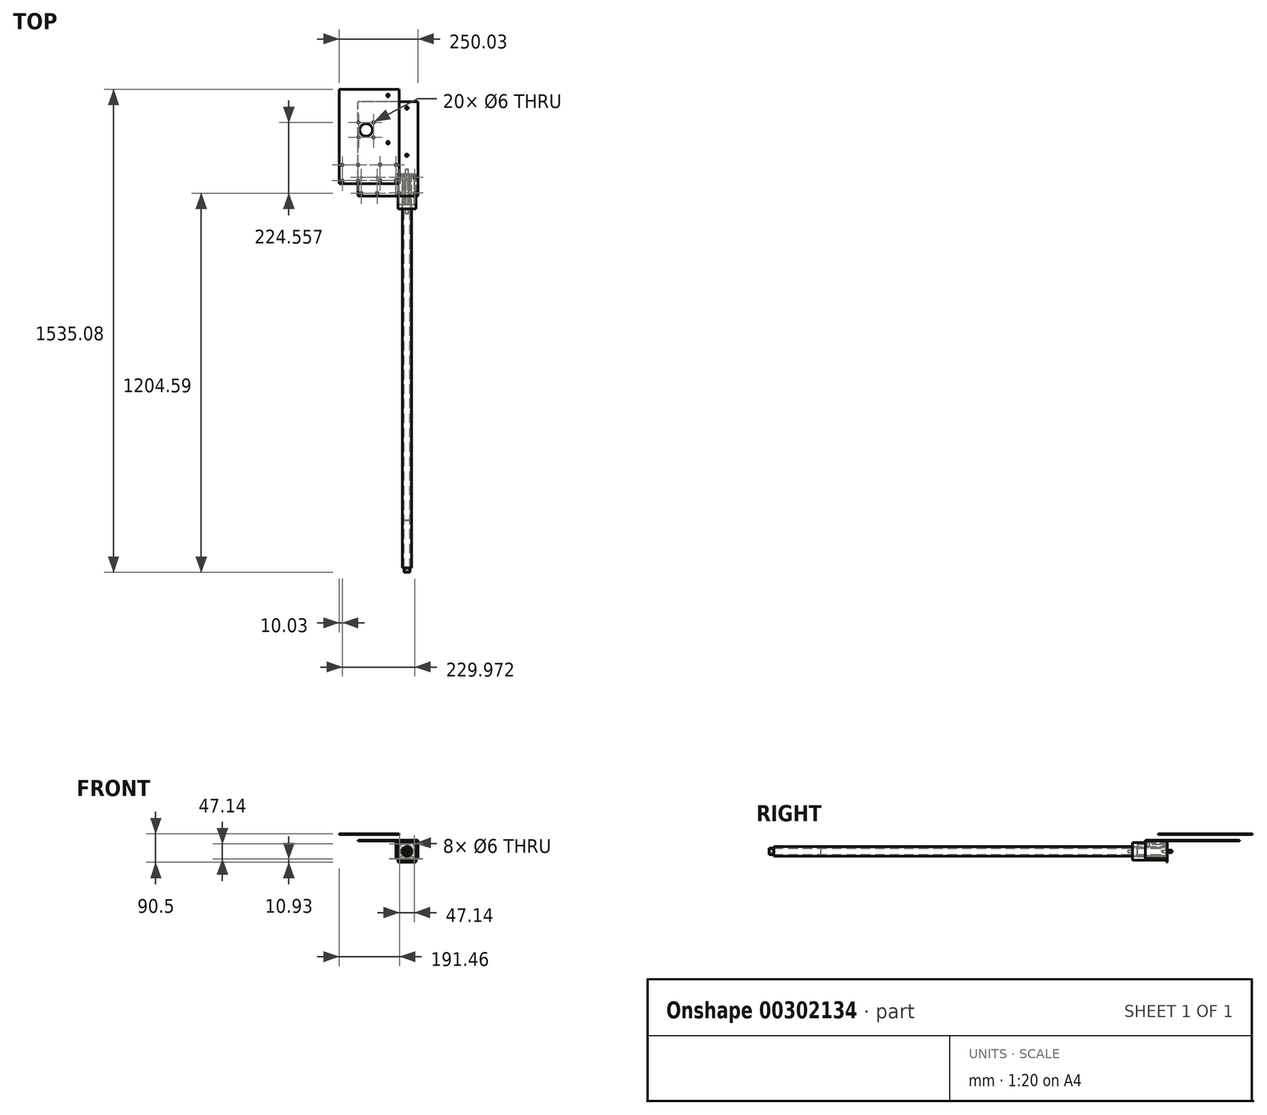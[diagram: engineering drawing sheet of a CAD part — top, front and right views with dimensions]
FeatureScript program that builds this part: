
annotation { "Feature Type Name" : "Feature", "Feature Type Description" : "" }
export const myFeature = defineFeature(function(context is Context, id is Id, definition is map)
    precondition{}
    {
        {
            var Q0;
            Q0=qCreatedBy(makeId("Front.planeOp"),FACE);
            var sketch = newSketch(context, id + "F0", { "sketchPlane" : qUnion([Q0])});
            skPoint(sketch, "E0.middle", {"position": v(0, 0) * mm});
            skLineSegment(sketch, "E1.bottom", {"start": v(28.5, 28.5) * mm, "end": v(-28.5, 28.5) * mm});
            skLineSegment(sketch, "E1.top", {"start": v(28.5, -28.5) * mm, "end": v(-28.5, -28.5) * mm});
            skLineSegment(sketch, "E1.left", {"start": v(28.5, 28.5) * mm, "end": v(28.5, -28.5) * mm});
            skLineSegment(sketch, "E1.right", {"start": v(-28.5, 28.5) * mm, "end": v(-28.5, -28.5) * mm});
            skCircle(sketch, "E2", {"center": v(0, 0) * mm, "radius": 4 * mm});
            skLineSegment(sketch, "E3.bottom", {"start": v(23.5, 23.5) * mm, "end": v(-23.5, 23.5) * mm, "construction": true});
            skLineSegment(sketch, "E3.top", {"start": v(23.5, -23.5) * mm, "end": v(-23.5, -23.5) * mm, "construction": true});
            skLineSegment(sketch, "E3.left", {"start": v(23.5, 23.5) * mm, "end": v(23.5, -23.5) * mm, "construction": true});
            skLineSegment(sketch, "E3.right", {"start": v(-23.5, 23.5) * mm, "end": v(-23.5, -23.5) * mm, "construction": true});
            skSolve(sketch);
        }
        {
            var Q0;
            Q0=makeQuery(id+"F0.imprint","IMPRINT",FACE,{"disambiguationData":[TD([[makeQuery(id+"F0.imprint","IMPRINT",EDGE,{"derivedFrom":sQuery(id+"F0.wireOp",EDGE,"E2")}),1.0]])]});
            var Q1;
            Q1=sQuery(id+"F0.wireOp",EDGE,"E2");
            extrude(context, id + "F1", {"entities" : qUnion([Q0]), "surfaceEntities" : qUnion([Q1]), "depth" : 125 * mm, "hasSecondDirection" : true, "secondDirectionOppositeDirection" : true, "secondDirectionDepth" : 15 * mm});
        }
        {
            var Q0;
            Q0=makeQuery(id+"F0.imprint","IMPRINT",FACE,{"disambiguationData":[TD([[makeQuery(id+"F0.imprint","IMPRINT",EDGE,{"derivedFrom":sQuery(id+"F0.wireOp",EDGE,"E1.bottom")}),1.0]])]});
            extrude(context, id + "F2", {"entities" : qUnion([Q0]), "operationType" : NewBodyOperationType.ADD, "depth" : 110 * mm});
        }
        {
            var Q0;
            Q0=sQuery(id+"F0.wireOp",VERTEX,"E3.left.end");
            var Q1;
            Q1=sQuery(id+"F0.wireOp",VERTEX,"E3.left.start");
            var Q2;
            Q2=sQuery(id+"F0.wireOp",VERTEX,"E3.right.start");
            var Q3;
            Q3=sQuery(id+"F0.wireOp",VERTEX,"E3.right.end");
            var Q4;
            Q4=makeQuery(id+"F1.opExtrude","SWEPT_BODY",BODY,{"disambiguationData":[OSD([sQuery(id+"F0.wireOp",EDGE,"E2")])]});
            hole(context, id + "F3", {"style" : HoleStyle.SIMPLE, "endStyle" : HoleEndStyle.BLIND, "oppositeDirection" : true, "standardTappedOrClearance" : lookupTablePath({ "standard" : "ISO", "size" : "6", "type" : "Drilled" }), "standardBlindInLast" : lookupTablePath({ "standard" : "ISO", "size" : "6", "type" : "Drilled" }), "holeDiameter" : 6 * mm, "holeDepth" : 16 * mm, "tappedDepth" : 12 * mm, "tapClearance" : 3, "locations" : qUnion([Q0, Q1, Q2, Q3]), "scope" : qUnion([Q4])});
        }
        {
            var Q0;
            Q0=qCreatedBy(makeId("Front.planeOp"),FACE);
            var sketch = newSketch(context, id + "F4", { "sketchPlane" : qUnion([Q0])});
            skCircle(sketch, "E4", {"center": v(0, 0) * mm, "radius": 12.5 * mm});
            skSolve(sketch);
        }
        {
            var Q0;
            Q0 = qSketchRegion(id + "F4", true);
            extrude(context, id + "F5", {"entities" : qUnion([Q0]), "depth" : (1100) * mm});
        }
        {
            var Q0;
            Q0=qCreatedBy(makeId("Front.planeOp"),FACE);
            var sketch = newSketch(context, id + "F6", { "sketchPlane" : qUnion([Q0])});
            skLineSegment(sketch, "E5.top", {"start": v(0, 33) * mm, "end": v(35, 33) * mm});
            skLineSegment(sketch, "E5.left", {"start": v(0, 15) * mm, "end": v(0, 33) * mm});
            skLineSegment(sketch, "E5.right", {"start": v(35, 0) * mm, "end": v(35, 33) * mm});
            skLineSegment(sketch, "E6.top", {"start": v(7, -23) * mm, "end": v(35, -23) * mm});
            skLineSegment(sketch, "E6.right", {"start": v(35, 0) * mm, "end": v(35, -23) * mm});
            skLineSegment(sketch, "E7.MirrorCS", {"start": v(0, 33) * mm, "end": v(-35, 33) * mm});
            skLineSegment(sketch, "E8.MirrorCS", {"start": v(-35, 0) * mm, "end": v(-35, 33) * mm});
            skLineSegment(sketch, "E9.MirrorCS", {"start": v(-35, 0) * mm, "end": v(-35, -23) * mm});
            skLineSegment(sketch, "E10.MirrorCS", {"start": v(-7, -23) * mm, "end": v(-35, -23) * mm});
            skCircle(sketch, "E11", {"center": v(0, 0) * mm, "radius": 15 * mm});
            skLineSegment(sketch, "E12", {"start": v(7, -23) * mm, "end": v(4.37, -14.35) * mm});
            skLineSegment(sketch, "E13", {"start": v(-4.37, -14.35) * mm, "end": v(-7, -23) * mm});
            skPoint(sketch, "E14.orphan", {"position": v(0, -23) * mm});
            skSolve(sketch);
        }
        {
            var Q0;
            Q0=makeQuery(id+"F6.imprint","IMPRINT",FACE,{"disambiguationData":[TD([[makeQuery(id+"F6.imprint","IMPRINT",EDGE,{"derivedFrom":sQuery(id+"F6.wireOp",EDGE,"E5.top")}),-1.0]])]});
            var Q1;
            {var subQ0=sQuery(id+"F6.wireOp",EDGE,"E5.left");Q1=makeQuery(id+"F6.imprint","IMPRINT",FACE,{"disambiguationData":[TD([[makeQuery(id+"F6.imprint","IMPRINT",EDGE,{"derivedFrom":subQ0}),1.0]])]});}
            extrude(context, id + "F7", {"entities" : qUnion([Q0, Q1]), "depth" : 70 * mm});
        }
        {
            var Q0;
            Q0=qCreatedBy(makeId("Front.planeOp"),FACE);
            var sketch = newSketch(context, id + "F8", { "sketchPlane" : qUnion([Q0])});
            skLineSegment(sketch, "E15.top", {"start": v(0, 23) * mm, "end": v(24, 23) * mm});
            skLineSegment(sketch, "E15.right", {"start": v(24, 0) * mm, "end": v(24, 23) * mm});
            skLineSegment(sketch, "E16.top", {"start": v(5, -16) * mm, "end": v(24, -16) * mm});
            skLineSegment(sketch, "E16.right", {"start": v(24, 0) * mm, "end": v(24, -16) * mm});
            skLineSegment(sketch, "E17.MirrorCS", {"start": v(0, 23) * mm, "end": v(-24, 23) * mm});
            skLineSegment(sketch, "E18.MirrorCS", {"start": v(-24, 0) * mm, "end": v(-24, 23) * mm});
            skLineSegment(sketch, "E19.MirrorCS", {"start": v(-24, 0) * mm, "end": v(-24, -16) * mm});
            skLineSegment(sketch, "E20.MirrorCS", {"start": v(-5, -16) * mm, "end": v(-24, -16) * mm});
            skArc(sketch, "E21", {"start": v(2.98, -9.54) * mm, "mid": v(0, 10) * mm, "end": v(-2.98, -9.54) * mm});
            skLineSegment(sketch, "E22", {"start": v(2.98, -9.54) * mm, "end": v(5, -16) * mm});
            skLineSegment(sketch, "E23", {"start": v(-5, -16) * mm, "end": v(-2.98, -9.54) * mm});
            skPoint(sketch, "E24.orphan", {"position": v(5, 0) * mm});
            skPoint(sketch, "E25.MirrorCS.start.orphan", {"position": v(-5, 0) * mm});
            skPoint(sketch, "E26.orphan", {"position": v(0, -16) * mm});
            skSolve(sketch);
        }
        {
            var Q0;
            Q0=makeQuery(id+"F8.imprint","IMPRINT",FACE,{"disambiguationData":[TD([[makeQuery(id+"F8.imprint","IMPRINT",EDGE,{"derivedFrom":sQuery(id+"F8.wireOp",EDGE,"E15.top")}),-1.0]])]});
            extrude(context, id + "F9", {"entities" : qUnion([Q0]), "depth" : 96 * mm});
        }
        {
            var Q0;
            Q0=makeQuery(id+"F7.opExtrude","SWEPT_FACE",FACE,{"disambiguationData":[OSD([sQuery(id+"F6.wireOp",EDGE,"E5.top"),sQuery(id+"F6.wireOp",EDGE,"E7.MirrorCS")])]});
            var sketch = newSketch(context, id + "F10", { "sketchPlane" : qUnion([Q0])});
            skLineSegment(sketch, "E27.bottom", {"start": v(-25, -10) * mm, "end": v(25, -10) * mm, "construction": true});
            skLineSegment(sketch, "E27.top", {"start": v(-25, -60) * mm, "end": v(25, -60) * mm, "construction": true});
            skLineSegment(sketch, "E27.left", {"start": v(-25, -10) * mm, "end": v(-25, -60) * mm, "construction": true});
            skLineSegment(sketch, "E27.right", {"start": v(25, -10) * mm, "end": v(25, -60) * mm, "construction": true});
            skSolve(sketch);
        }
        {
            var Q0;
            Q0=sQuery(id+"F10.wireOp",VERTEX,"E27.left.end");
            var Q1;
            Q1=sQuery(id+"F10.wireOp",VERTEX,"E27.bottom.start");
            var Q2;
            Q2=sQuery(id+"F10.wireOp",VERTEX,"E27.right.start");
            var Q3;
            Q3=sQuery(id+"F10.wireOp",VERTEX,"E27.right.end");
            var Q4;
            Q4=makeQuery(id+"F7.opExtrude","SWEPT_BODY",BODY,{"disambiguationData":[OSD([sQuery(id+"F6.wireOp",EDGE,"E5.top"),sQuery(id+"F6.wireOp",EDGE,"E5.right"),sQuery(id+"F6.wireOp",EDGE,"E6.top"),sQuery(id+"F6.wireOp",EDGE,"E6.right"),sQuery(id+"F6.wireOp",EDGE,"E7.MirrorCS"),sQuery(id+"F6.wireOp",EDGE,"E8.MirrorCS"),sQuery(id+"F6.wireOp",EDGE,"E9.MirrorCS"),sQuery(id+"F6.wireOp",EDGE,"E10.MirrorCS"),sQuery(id+"F6.wireOp",EDGE,"E11"),sQuery(id+"F6.wireOp",EDGE,"E12"),sQuery(id+"F6.wireOp",EDGE,"E13")])]});
            hole(context, id + "F11", {"style" : HoleStyle.SIMPLE, "endStyle" : HoleEndStyle.BLIND, "standardTappedOrClearance" : lookupTablePath({ "standard" : "ISO", "size" : "8", "type" : "Drilled" }), "standardBlindInLast" : lookupTablePath({ "standard" : "ISO", "size" : "8", "type" : "Drilled" }), "holeDiameter" : 8 * mm, "holeDepth" : 16 * mm, "tappedDepth" : 12 * mm, "tapClearance" : 3, "locations" : qUnion([Q0, Q1, Q2, Q3]), "scope" : qUnion([Q4])});
        }
        {
            var Q0;
            Q0=qCreatedBy(makeId("Front.planeOp"),FACE);
            var sketch = newSketch(context, id + "F12", { "sketchPlane" : qUnion([Q0])});
            skCircle(sketch, "E28", {"center": v(0, 0) * mm, "radius": 15 * mm});
            skSolve(sketch);
        }
        {
            var Q0;
            Q0=makeQuery(id+"F12.imprint","IMPRINT",FACE,{"disambiguationData":[TD([[makeQuery(id+"F12.imprint","IMPRINT",EDGE,{"derivedFrom":sQuery(id+"F12.wireOp",EDGE,"E28")}),1.0]])]});
            extrude(context, id + "F13", {"entities" : qUnion([Q0]), "depth" : 1250 * mm});
        }
        {
            var Q0;
            {var subQ0=sQuery(id+"F6.wireOp",EDGE,"E5.top");Q0=makeQuery(id+"F10.imprint","IMPRINT",FACE,{"disambiguationData":[TD([[makeQuery(id+"F10.imprint","IMPRINT",EDGE,{"derivedFrom":makeQuery(id+"F7.opExtrude","SWEPT_EDGE",EDGE,{"disambiguationData":[OSD([subQ0,sQuery(id+"F6.wireOp",EDGE,"E5.right")])]})}),1.0]])]});}
            var sketch = newSketch(context, id + "F14", { "sketchPlane" : qUnion([Q0])});
            skLineSegment(sketch, "E29.left", {"start": v(0, -59.92) * mm, "end": v(0, -9.92) * mm});
            skLineSegment(sketch, "E30.bottom", {"start": v(-145, -10.41) * mm, "end": v(-95, -10.41) * mm, "construction": true});
            skLineSegment(sketch, "E30.top", {"start": v(-145, -60.41) * mm, "end": v(-95, -60.41) * mm, "construction": true});
            skLineSegment(sketch, "E30.left", {"start": v(-145, -10.41) * mm, "end": v(-145, -60.41) * mm, "construction": true});
            skLineSegment(sketch, "E30.right", {"start": v(-95, -10.41) * mm, "end": v(-95, -60.41) * mm, "construction": true});
            skPoint(sketch, "E30.middle", {"position": v(-120, -35.41) * mm});
            skLineSegment(sketch, "E31.bottom", {"start": v(34.97, -69.92) * mm, "end": v(-155.03, -69.92) * mm});
            skLineSegment(sketch, "E31.top", {"start": v(34.97, 230.08) * mm, "end": v(-155.03, 230.08) * mm});
            skLineSegment(sketch, "E31.left", {"start": v(34.97, -69.92) * mm, "end": v(34.97, 230.08) * mm});
            skLineSegment(sketch, "E31.right", {"start": v(-155.03, -69.92) * mm, "end": v(-155.03, 230.08) * mm});
            skLineSegment(sketch, "E32", {"start": v(0, 0) * mm, "end": v(0, 230) * mm});
            skLineSegment(sketch, "E33.bottom", {"start": v(-20.03, 60.08) * mm, "end": v(-0.03, 60.08) * mm, "construction": true});
            skLineSegment(sketch, "E33.top", {"start": v(-20.03, 210.08) * mm, "end": v(-0.03, 210.08) * mm, "construction": true});
            skLineSegment(sketch, "E33.left", {"start": v(-20.03, 60.08) * mm, "end": v(-20.03, 210.08) * mm, "construction": true});
            skLineSegment(sketch, "E33.right", {"start": v(-0.03, 60.08) * mm, "end": v(-0.03, 210.08) * mm, "construction": true});
            skLineSegment(sketch, "E34.bottom", {"start": v(-25.03, -9.92) * mm, "end": v(24.97, -9.92) * mm, "construction": true});
            skLineSegment(sketch, "E34.top", {"start": v(-25.03, -59.92) * mm, "end": v(24.97, -59.92) * mm, "construction": true});
            skLineSegment(sketch, "E34.left", {"start": v(-25.03, -9.92) * mm, "end": v(-25.03, -59.92) * mm, "construction": true});
            skLineSegment(sketch, "E34.right", {"start": v(24.97, -9.92) * mm, "end": v(24.97, -59.92) * mm, "construction": true});
            skSolve(sketch);
        }
        {
            var Q0;
            {var subQ4=sQuery(id+"F14.wireOp",EDGE,"E31.bottom");var subQ6=sQuery(id+"F14.wireOp",EDGE,"E31.left");var subQ7=makeQuery(id+"F14.imprint","INTERSECT",VERTEX,{"derivedFrom":[subQ4,subQ6]});Q0=makeQuery(id+"F14.imprint","IMPRINT",FACE,{"disambiguationData":[TD([[makeQuery(id+"F14.imprint","IMPRINT",EDGE,{"disambiguationData":[TD([[subQ7,-1.0]])],"derivedFrom":subQ4}),-1.0]])]});}
            var Q1;
            {var subQ2=sQuery(id+"F14.wireOp",EDGE,"E31.top");Q1=makeQuery(id+"F14.imprint","IMPRINT",FACE,{"disambiguationData":[TD([[makeQuery(id+"F14.imprint","IMPRINT",EDGE,{"derivedFrom":subQ2}),1.0]])]});}
            extrude(context, id + "F15", {"entities" : qUnion([Q0, Q1]), "depth" : 3 * mm});
        }
        {
            var Q0;
            Q0=sQuery(id+"F14.wireOp",VERTEX,"E30.left.start");
            var Q1;
            Q1=sQuery(id+"F14.wireOp",VERTEX,"E30.right.start");
            var Q2;
            Q2=sQuery(id+"F14.wireOp",VERTEX,"E30.right.end");
            var Q3;
            Q3=sQuery(id+"F14.wireOp",VERTEX,"E30.left.end");
            var Q4;
            Q4=sQuery(id+"F14.wireOp",VERTEX,"E34.bottom.start");
            var Q5;
            Q5=sQuery(id+"F14.wireOp",VERTEX,"E34.top.start");
            var Q6;
            Q6=sQuery(id+"F14.wireOp",VERTEX,"E34.top.end");
            var Q7;
            Q7=sQuery(id+"F14.wireOp",VERTEX,"E34.right.start");
            var Q8;
            Q8=makeQuery(id+"F15.opExtrude","SWEPT_BODY",BODY,{"disambiguationData":[OSD([sQuery(id+"F14.wireOp",EDGE,"E31.bottom"),sQuery(id+"F14.wireOp",EDGE,"E31.top"),sQuery(id+"F14.wireOp",EDGE,"E31.left"),sQuery(id+"F14.wireOp",EDGE,"E31.right")])]});
            hole(context, id + "F16", {"style" : HoleStyle.SIMPLE, "endStyle" : HoleEndStyle.THROUGH, "oppositeDirection" : true, "standardTappedOrClearance" : lookupTablePath({ "standard" : "ISO", "size" : "6", "type" : "Drilled" }), "standardBlindInLast" : lookupTablePath({ "standard" : "ISO", "size" : "6", "type" : "Drilled" }), "holeDiameter" : 6 * mm, "tappedDepth" : 12 * mm, "tapClearance" : 3, "locations" : qUnion([Q0, Q1, Q2, Q3, Q4, Q5, Q6, Q7]), "scope" : qUnion([Q8])});
        }
        {
            var Q0;
            Q0=sQuery(id+"F14.wireOp",VERTEX,"E33.right.end");
            var Q1;
            Q1=sQuery(id+"F14.wireOp",VERTEX,"E33.bottom.end");
            var Q2;
            Q2=makeQuery(id+"F15.opExtrude","SWEPT_BODY",BODY,{"disambiguationData":[OSD([sQuery(id+"F14.wireOp",EDGE,"E31.bottom"),sQuery(id+"F14.wireOp",EDGE,"E31.top"),sQuery(id+"F14.wireOp",EDGE,"E31.left"),sQuery(id+"F14.wireOp",EDGE,"E31.right")])]});
            hole(context, id + "F17", {"style" : HoleStyle.SIMPLE, "endStyle" : HoleEndStyle.THROUGH, "oppositeDirection" : true, "standardTappedOrClearance" : lookupTablePath({ "standard" : "ISO", "size" : "8.5", "type" : "Drilled" }), "standardBlindInLast" : lookupTablePath({ "standard" : "ISO", "size" : "8.5", "type" : "Drilled" }), "holeDiameter" : 8.5 * mm, "tappedDepth" : 12 * mm, "tapClearance" : 3, "locations" : qUnion([Q0, Q1]), "scope" : qUnion([Q2])});
        }
        {
            var Q0;
            Q0=qCreatedBy(makeId("Front.planeOp"),FACE);
            var sketch = newSketch(context, id + "F18", { "sketchPlane" : qUnion([Q0])});
            skCircle(sketch, "E35", {"center": v(0, 0) * mm, "radius": 10 * mm});
            skSolve(sketch);
        }
        {
            var Q0;
            Q0 = qSketchRegion(id + "F18", true);
            extrude(context, id + "F19", {"entities" : qUnion([Q0]), "depth" : 1265 * mm});
        }
        {
            var Q0;
            Q0=sQuery(id+"F18.wireOp",VERTEX,"E35.center");
            var Q1;
            Q1=makeQuery(id+"F19.opExtrude","SWEPT_BODY",BODY,{"disambiguationData":[OSD([sQuery(id+"F18.wireOp",EDGE,"E35")])]});
            hole(context, id + "F20", {"style" : HoleStyle.SIMPLE, "endStyle" : HoleEndStyle.BLIND, "oppositeDirection" : true, "standardTappedOrClearance" : lookupTablePath({ "standard" : "ISO", "fit" : "Normal", "size" : "M8", "type" : "Clearance" }), "standardBlindInLast" : lookupTablePath({ "fit" : "Standard", "standard" : "ISO", "size" : "M8", "type" : "Clearance" }), "holeDiameter" : 8.8 * mm, "holeDepth" : 15.75 * mm, "tappedDepth" : 12 * mm, "tapClearance" : 3, "locations" : qUnion([Q0]), "scope" : qUnion([Q1])});
        }
        {
            var Q0;
            Q0=makeQuery(id+"F19.opExtrude","CAP_FACE",FACE,{"disambiguationData":[OSD([sQuery(id+"F18.wireOp",EDGE,"E35")])],"isStart":false});
            cPlane(context, id + "F21", {"entities" : qUnion([Q0]), "cplaneType" : CPlaneType.OFFSET, "offset" : 0 * mm, "width" : 150 * mm, "height" : 150 * mm});
        }
        {
            var Q0;
            Q0=qCreatedBy(id+"F21.planeOp",FACE);
            var sketch = newSketch(context, id + "F22", { "sketchPlane" : qUnion([Q0])});
            skPoint(sketch, "E36", {"position": v(0, 0) * mm});
            skSolve(sketch);
        }
        {
            var Q0;
            Q0=sQuery(id+"F22.wireOp",VERTEX,"E36");
            var Q1;
            Q1=makeQuery(id+"F19.opExtrude","SWEPT_BODY",BODY,{"disambiguationData":[OSD([sQuery(id+"F18.wireOp",EDGE,"E35")])]});
            hole(context, id + "F23", {"style" : HoleStyle.SIMPLE, "endStyle" : HoleEndStyle.BLIND, "standardTappedOrClearance" : lookupTablePath({ "standard" : "ISO", "engagement" : "75%", "pitch" : "1.25 mm", "size" : "M8", "type" : "Tapped" }), "standardBlindInLast" : lookupTablePath({ "standard" : "ISO", "engagement" : "75%", "pitch" : "1.25 mm", "size" : "M8", "type" : "Tapped" }), "holeDiameter" : 6.8 * mm, "showTappedDepth" : true, "holeDepth" : 15.75 * mm, "tappedDepth" : 12 * mm, "tapClearance" : 3, "startFromSketch" : true, "locations" : qUnion([Q0]), "scope" : qUnion([Q1]), "majorDiameter" : 8 * mm});
        }
        {
            var Q0;
            Q0=qCreatedBy(makeId("Front.planeOp"),FACE);
            var sketch = newSketch(context, id + "F24", { "sketchPlane" : qUnion([Q0])});
            skLineSegment(sketch, "E37.bottom", {"start": v(23.57, -23.57) * mm, "end": v(-23.57, -23.57) * mm, "construction": true});
            skLineSegment(sketch, "E37.top", {"start": v(23.57, 23.57) * mm, "end": v(-23.57, 23.57) * mm, "construction": true});
            skLineSegment(sketch, "E37.left", {"start": v(23.57, -23.57) * mm, "end": v(23.57, 23.57) * mm, "construction": true});
            skLineSegment(sketch, "E37.right", {"start": v(-23.57, -23.57) * mm, "end": v(-23.57, 23.57) * mm, "construction": true});
            skPoint(sketch, "E37.middle", {"position": v(0, 0) * mm});
            skCircle(sketch, "E38", {"center": v(0, 0) * mm, "radius": 20 * mm});
            skLineSegment(sketch, "E39.bottom", {"start": v(-28.5, 28.5) * mm, "end": v(28.5, 28.5) * mm});
            skLineSegment(sketch, "E39.left", {"start": v(-28.5, 28.5) * mm, "end": v(-28.5, -31.5) * mm});
            skLineSegment(sketch, "E39.right", {"start": v(28.5, 28.5) * mm, "end": v(28.5, -31.5) * mm});
            skLineSegment(sketch, "E40.0", {"start": v(-28.5, -34.5) * mm, "end": v(28.5, -34.5) * mm});
            skLineSegment(sketch, "E41", {"start": v(-28.5, -31.5) * mm, "end": v(-28.5, -34.5) * mm});
            skLineSegment(sketch, "E42", {"start": v(28.5, -31.5) * mm, "end": v(28.5, -34.5) * mm});
            skSolve(sketch);
        }
        {
            var Q0;
            Q0=makeQuery(id+"F24.imprint","IMPRINT",FACE,{"disambiguationData":[TD([[makeQuery(id+"F24.imprint","IMPRINT",EDGE,{"derivedFrom":sQuery(id+"F24.wireOp",EDGE,"E38")}),-1.0]])]});
            extrude(context, id + "F25", {"entities" : qUnion([Q0]), "depth" : 3 * mm});
        }
        {
            var Q0;
            Q0=sQuery(id+"F24.wireOp",VERTEX,"E37.top.end");
            var Q1;
            Q1=sQuery(id+"F24.wireOp",VERTEX,"E37.top.start");
            var Q2;
            Q2=sQuery(id+"F24.wireOp",VERTEX,"E37.left.start");
            var Q3;
            Q3=sQuery(id+"F24.wireOp",VERTEX,"E37.bottom.end");
            var Q4;
            Q4=makeQuery(id+"F25.opExtrude","SWEPT_BODY",BODY,{"disambiguationData":[OSD([sQuery(id+"F24.wireOp",EDGE,"E38"),sQuery(id+"F24.wireOp",EDGE,"E39.bottom"),sQuery(id+"F24.wireOp",EDGE,"E39.left"),sQuery(id+"F24.wireOp",EDGE,"E39.right"),sQuery(id+"F24.wireOp",EDGE,"E40.0"),sQuery(id+"F24.wireOp",EDGE,"E41"),sQuery(id+"F24.wireOp",EDGE,"E42")])]});
            hole(context, id + "F26", {"style" : HoleStyle.SIMPLE, "endStyle" : HoleEndStyle.THROUGH, "oppositeDirection" : true, "standardTappedOrClearance" : lookupTablePath({ "standard" : "ISO", "size" : "6", "type" : "Drilled" }), "standardBlindInLast" : lookupTablePath({ "standard" : "ISO", "size" : "6", "type" : "Drilled" }), "holeDiameter" : 6 * mm, "tappedDepth" : 12 * mm, "tapClearance" : 3, "startFromSketch" : true, "locations" : qUnion([Q0, Q1, Q2, Q3]), "scope" : qUnion([Q4])});
        }
        {
            var Q0;
            Q0=makeQuery(id+"F15.opExtrude","SWEPT_BODY",BODY,{"disambiguationData":[OSD([sQuery(id+"F14.wireOp",EDGE,"E31.bottom"),sQuery(id+"F14.wireOp",EDGE,"E31.top"),sQuery(id+"F14.wireOp",EDGE,"E31.left"),sQuery(id+"F14.wireOp",EDGE,"E31.right")])]});
            var Q1;
            Q1=makeQuery(id+"F25.opExtrude","CAP_EDGE",EDGE,{"disambiguationData":[OSD([sQuery(id+"F24.wireOp",EDGE,"E40.0")])],"isStart":false});
            transform(context, id + "F27", {"entities" : qUnion([Q0]), "transformType" : TransformType.TRANSLATION_3D, "dx" : -60 * mm, "dy" : 40 * mm, "dz" : 20 * mm, "makeCopy" : true});
        }
        {
            var Q0;
            Q0=makeQuery(id+"F27.opPattern","COPY",FACE,{"derivedFrom":makeQuery(id+"F15.opExtrude","CAP_FACE",FACE,{"disambiguationData":[OSD([sQuery(id+"F14.wireOp",EDGE,"E31.bottom"),sQuery(id+"F14.wireOp",EDGE,"E31.top"),sQuery(id+"F14.wireOp",EDGE,"E31.left"),sQuery(id+"F14.wireOp",EDGE,"E31.right")])],"isStart":false}),"instanceName":"1"});
            var sketch = newSketch(context, id + "F28", { "sketchPlane" : qUnion([Q0])});
            skLineSegment(sketch, "E43.bottom", {"start": v(-106.24, 117) * mm, "end": v(-153.38, 117) * mm, "construction": true});
            skLineSegment(sketch, "E43.top", {"start": v(-106.24, 164.15) * mm, "end": v(-153.38, 164.15) * mm, "construction": true});
            skLineSegment(sketch, "E43.left", {"start": v(-106.24, 117) * mm, "end": v(-106.24, 164.15) * mm, "construction": true});
            skLineSegment(sketch, "E43.right", {"start": v(-153.38, 117) * mm, "end": v(-153.38, 164.15) * mm, "construction": true});
            skCircle(sketch, "E44", {"center": v(-129.8, 140.58) * mm, "radius": 20 * mm});
            skLineSegment(sketch, "E45.bottom", {"start": v(-158.3, 169.08) * mm, "end": v(-101.3, 169.08) * mm});
            skLineSegment(sketch, "E45.left", {"start": v(-158.3, 179.42) * mm, "end": v(-158.3, 169.08) * mm});
            skLineSegment(sketch, "E45.right", {"start": v(-101.3, 179.42) * mm, "end": v(-101.3, 169.08) * mm});
            skLineSegment(sketch, "E46.0", {"start": v(-158.3, 106.08) * mm, "end": v(-101.3, 106.08) * mm});
            skLineSegment(sketch, "E47", {"start": v(-158.3, 179.42) * mm, "end": v(-158.3, 106.08) * mm});
            skLineSegment(sketch, "E48", {"start": v(-101.3, 179.42) * mm, "end": v(-101.3, 106.08) * mm});
            skSolve(sketch);
        }
        {
            var Q0;
            Q0=sQuery(id+"F28.wireOp",VERTEX,"E43.right.start");
            var Q1;
            Q1=sQuery(id+"F28.wireOp",VERTEX,"E43.right.end");
            var Q2;
            Q2=sQuery(id+"F28.wireOp",VERTEX,"E43.left.end");
            var Q3;
            Q3=sQuery(id+"F28.wireOp",VERTEX,"E43.bottom.start");
            var Q4;
            Q4=makeQuery(id+"F27.opPattern","COPY",BODY,{"derivedFrom":makeQuery(id+"F15.opExtrude","SWEPT_BODY",BODY,{"disambiguationData":[OSD([sQuery(id+"F14.wireOp",EDGE,"E31.bottom"),sQuery(id+"F14.wireOp",EDGE,"E31.top"),sQuery(id+"F14.wireOp",EDGE,"E31.left"),sQuery(id+"F14.wireOp",EDGE,"E31.right")])]}),"instanceName":"1"});
            hole(context, id + "F29", {"style" : HoleStyle.SIMPLE, "endStyle" : HoleEndStyle.THROUGH, "standardTappedOrClearance" : lookupTablePath({ "standard" : "ISO", "size" : "6", "type" : "Drilled" }), "standardBlindInLast" : lookupTablePath({ "standard" : "ISO", "size" : "6", "type" : "Drilled" }), "holeDiameter" : 6 * mm, "tappedDepth" : 12 * mm, "tapClearance" : 3, "startFromSketch" : true, "locations" : qUnion([Q0, Q1, Q2, Q3]), "scope" : qUnion([Q4])});
        }
        {
            var Q0;
            Q0=sQuery(id+"F28.wireOp",VERTEX,"E44.center");
            var Q1;
            Q1=makeQuery(id+"F27.opPattern","COPY",BODY,{"derivedFrom":makeQuery(id+"F15.opExtrude","SWEPT_BODY",BODY,{"disambiguationData":[OSD([sQuery(id+"F14.wireOp",EDGE,"E31.bottom"),sQuery(id+"F14.wireOp",EDGE,"E31.top"),sQuery(id+"F14.wireOp",EDGE,"E31.left"),sQuery(id+"F14.wireOp",EDGE,"E31.right")])]}),"instanceName":"1"});
            hole(context, id + "F30", {"style" : HoleStyle.SIMPLE, "endStyle" : HoleEndStyle.THROUGH, "holeDiameter" : 40 * mm, "tappedDepth" : 12 * mm, "tapClearance" : 3, "startFromSketch" : true, "locations" : qUnion([Q0]), "scope" : qUnion([Q1])});
        }
    });
